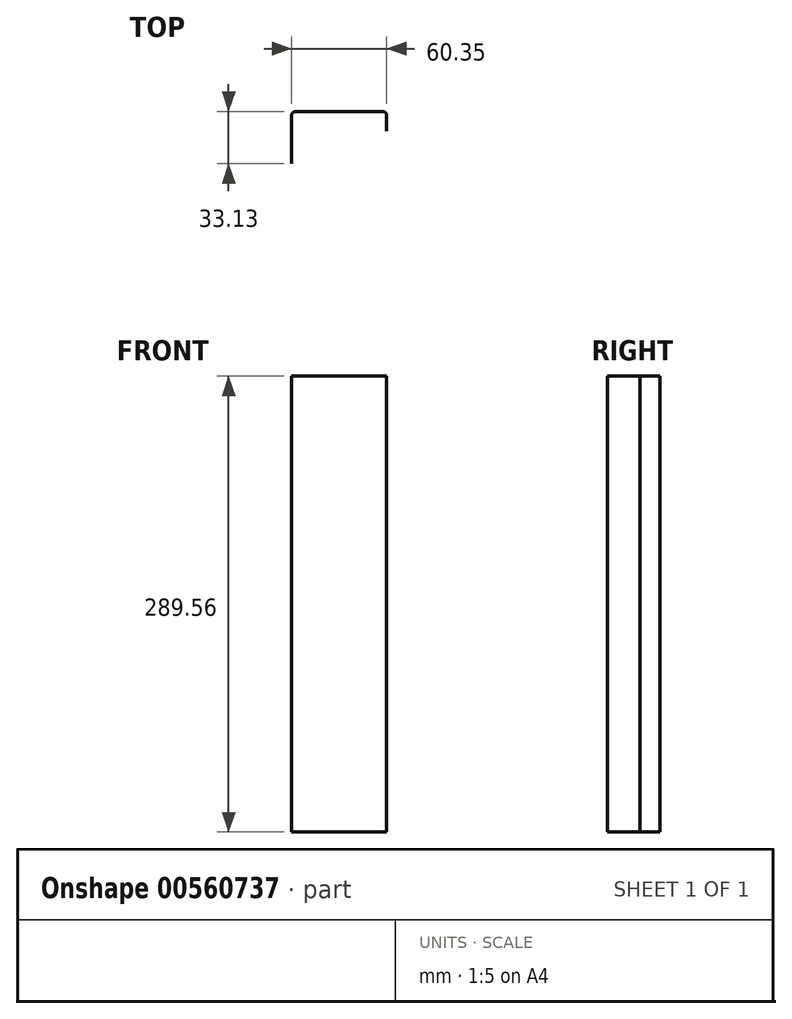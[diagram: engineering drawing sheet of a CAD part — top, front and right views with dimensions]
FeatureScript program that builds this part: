
annotation { "Feature Type Name" : "Feature", "Feature Type Description" : "" }
export const myFeature = defineFeature(function(context is Context, id is Id, definition is map)
    precondition{}
    {
        {
            var Q0;
            Q0=qCreatedBy(makeId("Top.planeOp"),FACE);
            var sketch = newSketch(context, id + "F0", { "sketchPlane" : qUnion([Q0])});
            skLineSegment(sketch, "E0", {"start": v(-34.33, 0) * mm, "end": v(-34.33, 33.13) * mm});
            skLineSegment(sketch, "E1", {"start": v(-34.33, 33.13) * mm, "end": v(26.02, 33.13) * mm});
            skLineSegment(sketch, "E2", {"start": v(26.02, 33.13) * mm, "end": v(26.02, 20.58) * mm});
            skSolve(sketch);
        }
        {
            var Q0;
            Q0 = qSketchRegion(id + "F0", true);
            var Q1;
            Q1=sQuery(id+"F0.wireOp",EDGE,"E2");
            var Q2;
            Q2=sQuery(id+"F0.wireOp",EDGE,"E1");
            var Q3;
            Q3=sQuery(id+"F0.wireOp",EDGE,"E0");
            extrude(context, id + "F1", {"entities" : qUnion([Q0]), "bodyType" : ToolBodyType.SURFACE, "surfaceEntities" : qUnion([Q1, Q2, Q3]), "depth" : 289.56 * mm, "offsetDistance" : 25.4 * mm});
        }
        {
            var Q0;
            Q0=makeQuery(id+"F1.opExtrude","SWEPT_EDGE",EDGE,{"disambiguationData":[OSD([sQuery(id+"F0.wireOp",VERTEX,"E1.end")])]});
            var Q1;
            Q1=makeQuery(id+"F1.opExtrude","SWEPT_EDGE",EDGE,{"disambiguationData":[OSD([sQuery(id+"F0.wireOp",VERTEX,"E0.end")])]});
            fillet(context, id + "F2", {"entities" : qUnion([Q0, Q1]), "radius" : 2.54 * mm, "tangentPropagation" : true, "allowEdgeOverflow" : false});
        }
    });
